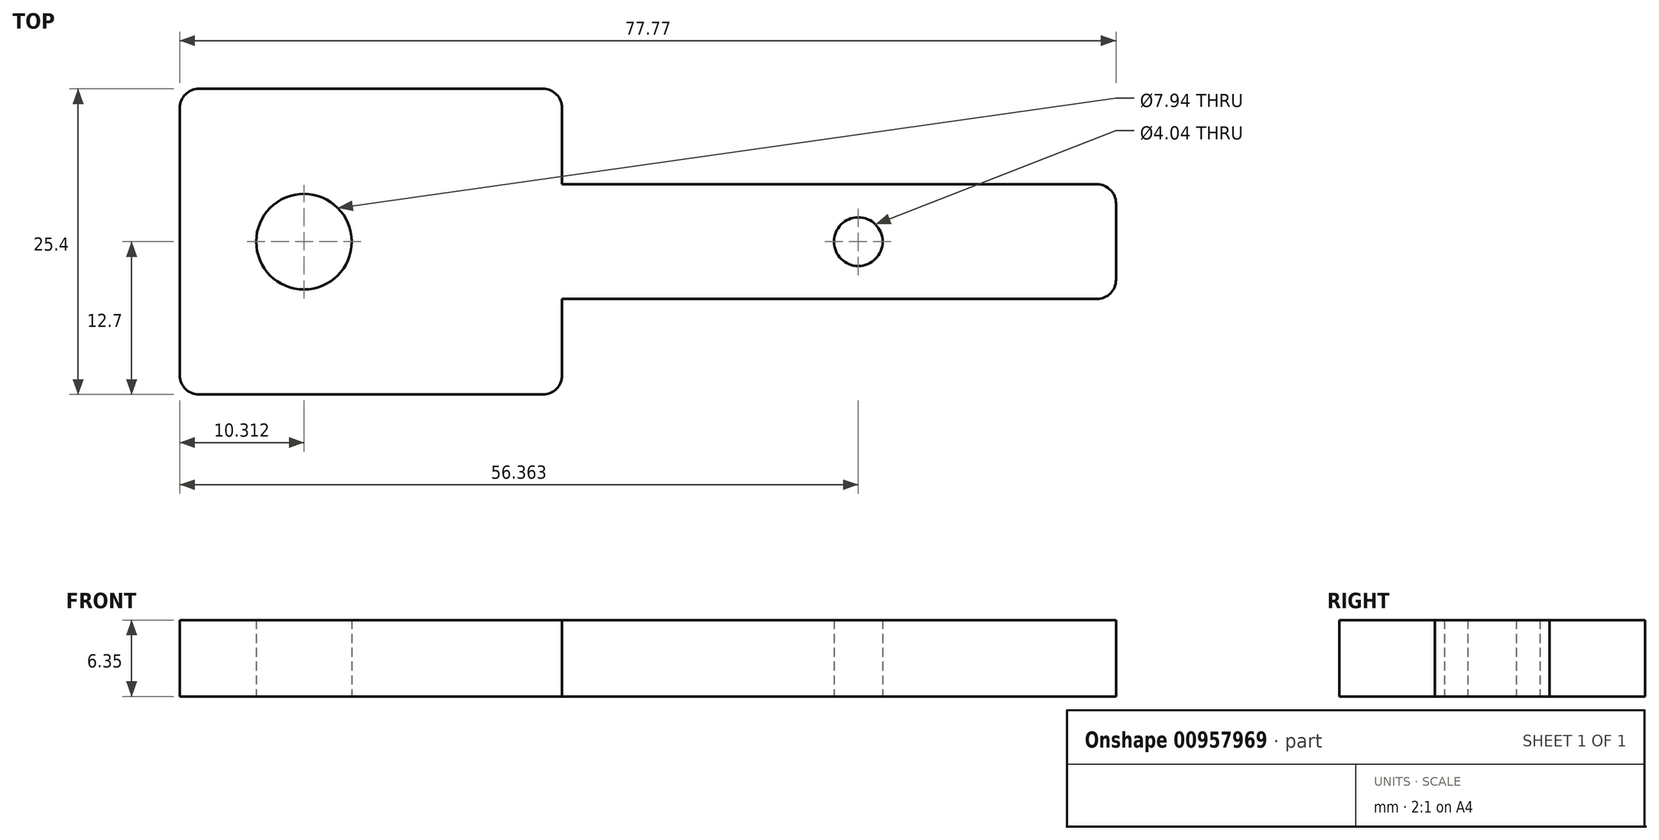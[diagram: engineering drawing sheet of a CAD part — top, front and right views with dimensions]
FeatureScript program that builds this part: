
annotation { "Feature Type Name" : "Feature", "Feature Type Description" : "" }
export const myFeature = defineFeature(function(context is Context, id is Id, definition is map)
    precondition{}
    {
        {
            var Q0;
            Q0=qCreatedBy(makeId("Top.planeOp"),FACE);
            var sketch = newSketch(context, id + "F0", { "sketchPlane" : qUnion([Q0])});
            skLineSegment(sketch, "E0", {"start": v(1.59, 0) * mm, "end": v(30.16, 0) * mm});
            skLineSegment(sketch, "E1", {"start": v(31.75, -1.59) * mm, "end": v(31.75, -7.94) * mm});
            skLineSegment(sketch, "E2", {"start": v(31.75, -7.94) * mm, "end": v(76.19, -7.94) * mm});
            skLineSegment(sketch, "E3", {"start": v(77.77, -9.53) * mm, "end": v(77.77, -15.88) * mm});
            skLineSegment(sketch, "E4", {"start": v(76.19, -17.46) * mm, "end": v(31.75, -17.46) * mm});
            skLineSegment(sketch, "E5", {"start": v(31.75, -17.46) * mm, "end": v(31.75, -23.81) * mm});
            skLineSegment(sketch, "E6", {"start": v(30.16, -25.4) * mm, "end": v(1.59, -25.4) * mm});
            skLineSegment(sketch, "E7", {"start": v(0, -23.81) * mm, "end": v(0, -1.59) * mm});
            skPoint(sketch, "E8.visualSharp", {"position": v(0, 0) * mm});
            skArc(sketch, "E8.filletArc", {"start": v(1.59, 0) * mm, "mid": v(0.46, -0.46) * mm, "end": v(0, -1.59) * mm});
            skPoint(sketch, "E9.visualSharp", {"position": v(0, -25.4) * mm});
            skArc(sketch, "E9.filletArc", {"start": v(0, -23.81) * mm, "mid": v(0.46, -24.94) * mm, "end": v(1.59, -25.4) * mm});
            skPoint(sketch, "E10.visualSharp", {"position": v(31.75, 0) * mm});
            skArc(sketch, "E10.filletArc", {"start": v(31.75, -1.59) * mm, "mid": v(31.29, -0.46) * mm, "end": v(30.16, 0) * mm});
            skPoint(sketch, "E11.visualSharp", {"position": v(31.75, -25.4) * mm});
            skArc(sketch, "E11.filletArc", {"start": v(30.16, -25.4) * mm, "mid": v(31.29, -24.94) * mm, "end": v(31.75, -23.81) * mm});
            skPoint(sketch, "E12.visualSharp", {"position": v(77.77, -7.94) * mm});
            skArc(sketch, "E12.filletArc", {"start": v(77.77, -9.53) * mm, "mid": v(77.3, -8.4) * mm, "end": v(76.19, -7.94) * mm});
            skPoint(sketch, "E13.visualSharp", {"position": v(77.77, -17.46) * mm});
            skArc(sketch, "E13.filletArc", {"start": v(76.19, -17.46) * mm, "mid": v(77.3, -17) * mm, "end": v(77.77, -15.88) * mm});
            skPoint(sketch, "E14", {"position": v(10.31, -12.7) * mm});
            skPoint(sketch, "E14.positionSnap0", {"position": v(0, -12.7) * mm});
            skPoint(sketch, "E15", {"position": v(56.36, -12.7) * mm});
            skPoint(sketch, "E15.positionSnap0", {"position": v(77.77, -12.7) * mm});
            skSolve(sketch);
        }
        {
            var Q0;
            Q0=makeQuery(id+"F0.imprint","IMPRINT",FACE,{"disambiguationData":[TD([[makeQuery(id+"F0.imprint","IMPRINT",EDGE,{"derivedFrom":sQuery(id+"F0.wireOp",EDGE,"E0")}),-1.0]])]});
            extrude(context, id + "F1", {"entities" : qUnion([Q0]), "depth" : 6.35 * mm, "offsetDistance" : 25.4 * mm});
        }
        {
            var Q0;
            Q0=sQuery(id+"F0.wireOp",VERTEX,"E14");
            var Q1;
            Q1=makeQuery(id+"F1.opExtrude","SWEPT_BODY",BODY,{"disambiguationData":[OSD([sQuery(id+"F0.wireOp",EDGE,"E0"),sQuery(id+"F0.wireOp",EDGE,"E1"),sQuery(id+"F0.wireOp",EDGE,"E2"),sQuery(id+"F0.wireOp",EDGE,"E3"),sQuery(id+"F0.wireOp",EDGE,"E4"),sQuery(id+"F0.wireOp",EDGE,"E5"),sQuery(id+"F0.wireOp",EDGE,"E6"),sQuery(id+"F0.wireOp",EDGE,"E7"),sQuery(id+"F0.wireOp",EDGE,"E9.filletArc"),sQuery(id+"F0.wireOp",EDGE,"E8.filletArc"),sQuery(id+"F0.wireOp",EDGE,"E10.filletArc"),sQuery(id+"F0.wireOp",EDGE,"E11.filletArc"),sQuery(id+"F0.wireOp",EDGE,"E12.filletArc"),sQuery(id+"F0.wireOp",EDGE,"E13.filletArc")])]});
            hole(context, id + "F2", {"style" : HoleStyle.SIMPLE, "endStyle" : HoleEndStyle.THROUGH, "oppositeDirection" : true, "standardTappedOrClearance" : lookupTablePath({ "standard" : "ANSI", "engagement" : "75%", "pitch" : "16 tpi", "size" : "3/8", "type" : "Tapped" }), "standardBlindInLast" : lookupTablePath({ "standard" : "ANSI", "fit" : "Normal", "engagement" : "75%", "pitch" : "16 tpi", "size" : "3/8", "type" : "Clearance & tapped" }), "holeDiameter" : 7.94 * mm, "majorDiameter" : 9.52 * mm, "showTappedDepth" : true, "isTappedThrough" : true, "tappedDepth" : 12.7 * mm, "tapClearance" : 3, "locations" : qUnion([Q0]), "scope" : qUnion([Q1])});
        }
        {
            var Q0;
            Q0=sQuery(id+"F0.wireOp",VERTEX,"E15");
            var Q1;
            Q1=makeQuery(id+"F1.opExtrude","SWEPT_BODY",BODY,{"disambiguationData":[OSD([sQuery(id+"F0.wireOp",EDGE,"E0"),sQuery(id+"F0.wireOp",EDGE,"E1"),sQuery(id+"F0.wireOp",EDGE,"E2"),sQuery(id+"F0.wireOp",EDGE,"E3"),sQuery(id+"F0.wireOp",EDGE,"E4"),sQuery(id+"F0.wireOp",EDGE,"E5"),sQuery(id+"F0.wireOp",EDGE,"E6"),sQuery(id+"F0.wireOp",EDGE,"E7"),sQuery(id+"F0.wireOp",EDGE,"E9.filletArc"),sQuery(id+"F0.wireOp",EDGE,"E8.filletArc"),sQuery(id+"F0.wireOp",EDGE,"E10.filletArc"),sQuery(id+"F0.wireOp",EDGE,"E11.filletArc"),sQuery(id+"F0.wireOp",EDGE,"E12.filletArc"),sQuery(id+"F0.wireOp",EDGE,"E13.filletArc")])]});
            hole(context, id + "F3", {"style" : HoleStyle.SIMPLE, "endStyle" : HoleEndStyle.THROUGH, "oppositeDirection" : true, "standardTappedOrClearance" : lookupTablePath({ "standard" : "ANSI", "engagement" : "75%", "pitch" : "32 tpi", "size" : "#10", "type" : "Tapped" }), "standardBlindInLast" : lookupTablePath({ "standard" : "ANSI", "fit" : "Normal", "engagement" : "75%", "pitch" : "32 tpi", "size" : "#10", "type" : "Clearance & tapped" }), "holeDiameter" : 4.04 * mm, "majorDiameter" : 4.83 * mm, "showTappedDepth" : true, "isTappedThrough" : true, "tappedDepth" : 12.7 * mm, "tapClearance" : 3, "locations" : qUnion([Q0]), "scope" : qUnion([Q1])});
        }
    });
